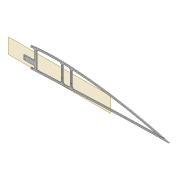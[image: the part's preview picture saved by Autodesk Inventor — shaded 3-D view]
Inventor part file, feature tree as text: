
AUTODESK INVENTOR PART (.ipt)
format: ipt  version: 2022 (Build 260153000, 153)  size: 561,152 bytes
history: native  units: mm
features: sketch x9, projected_geometry x9, extrude x8, fillet x2, shell x1, plane x1, chamfer x1
ambient origin geometry x8: Origin, YZ Plane, XZ Plane, XY Plane, X Axis, Y Axis, Z Axis, Center Point
bodies: Solid1 (feature_tree)
feature tree (31):
  extrude  "Extrusion1"  Depth=4.0mm
  shell  "Shell1"  Thickness=2.0mm
  extrude  "Extrusion8"  Depth=5.9mm
  extrude  "Extrusion3"  Depth=10.0mm TaperAngle=0.0deg
  extrude  "Extrusion4"  Depth=2.0mm
  fillet  "Fillet1"  Radius=80.0mm
  sketch  "Sketch10"  dims[d22=2.0mm d23=0.0mm d31=2.0mm d62=80.0mm]
  extrude  "Extrusion5"  Depth=2.0mm TaperAngle=0.0deg
  plane  "Work Plane2"
  extrude  "Extrusion10"  Depth=12.0mm
  fillet  "Fillet2"  Radius=5.0mm
  extrude  "Extrusion11"  Depth=12.0mm
  chamfer  "Chamfer1"  Distance=5.0mm
  extrude  "Extrusion13"  Depth=10.0mm TaperAngle=0.0deg
  sketch  "Sketch31"  dims[d75=30.0mm]
  sketch  "Sketch32"  dims[d76=3.05mm d77=5.0mm d78=10.0mm d79=0.0mm d80=2.0mm d81=100.0mm d82=20.0mm d83=1.6mm d84=1.6mm d85=2.5mm d86=2.5mm d87=0.5mm d88=10.0mm d89=0.0mm d92=10.0mm d93=10.0mm d94=3.0mm d95=2.0mm d96=45.0deg d98=1.0mm d99=1.0mm d100=1.0mm d101=1.0mm d102=1.0mm d103=1.0mm d104=10.0mm d105=0.0mm]
  sketch  "Sketch3"  dims[d0=2.0mm d1=0.0mm d2=4.0mm d7=2.0mm]
  sketch  "Sketch8"  dims[d8=2.0mm d9=5.9mm]
  sketch  "Sketch9"  dims[d13=10.0mm d14=0.0mm d16=10.0mm d17=0.0mm]
  projected_geometry  "Projected Loop4"
  projected_geometry  "Projected Loop10"
  sketch  "Sketch24"  dims[d63=6.0mm d64=2.0mm d65=0.0mm]
  projected_geometry  "Projected Loop11"
  projected_geometry  "Projected Loop12"
  projected_geometry  "Projected Loop13"
  sketch  "Sketch28"  dims[d66=3.0mm d67=12.0mm d68=5.0mm]
  projected_geometry  "Projected Loop14"
  sketch  "Sketch30"  dims[d69=5.0mm d74=12.0mm]
  projected_geometry  "Project Cut Edges1"
  projected_geometry  "Project Cut Edges2"
  projected_geometry  "Project Cut Edges3"
